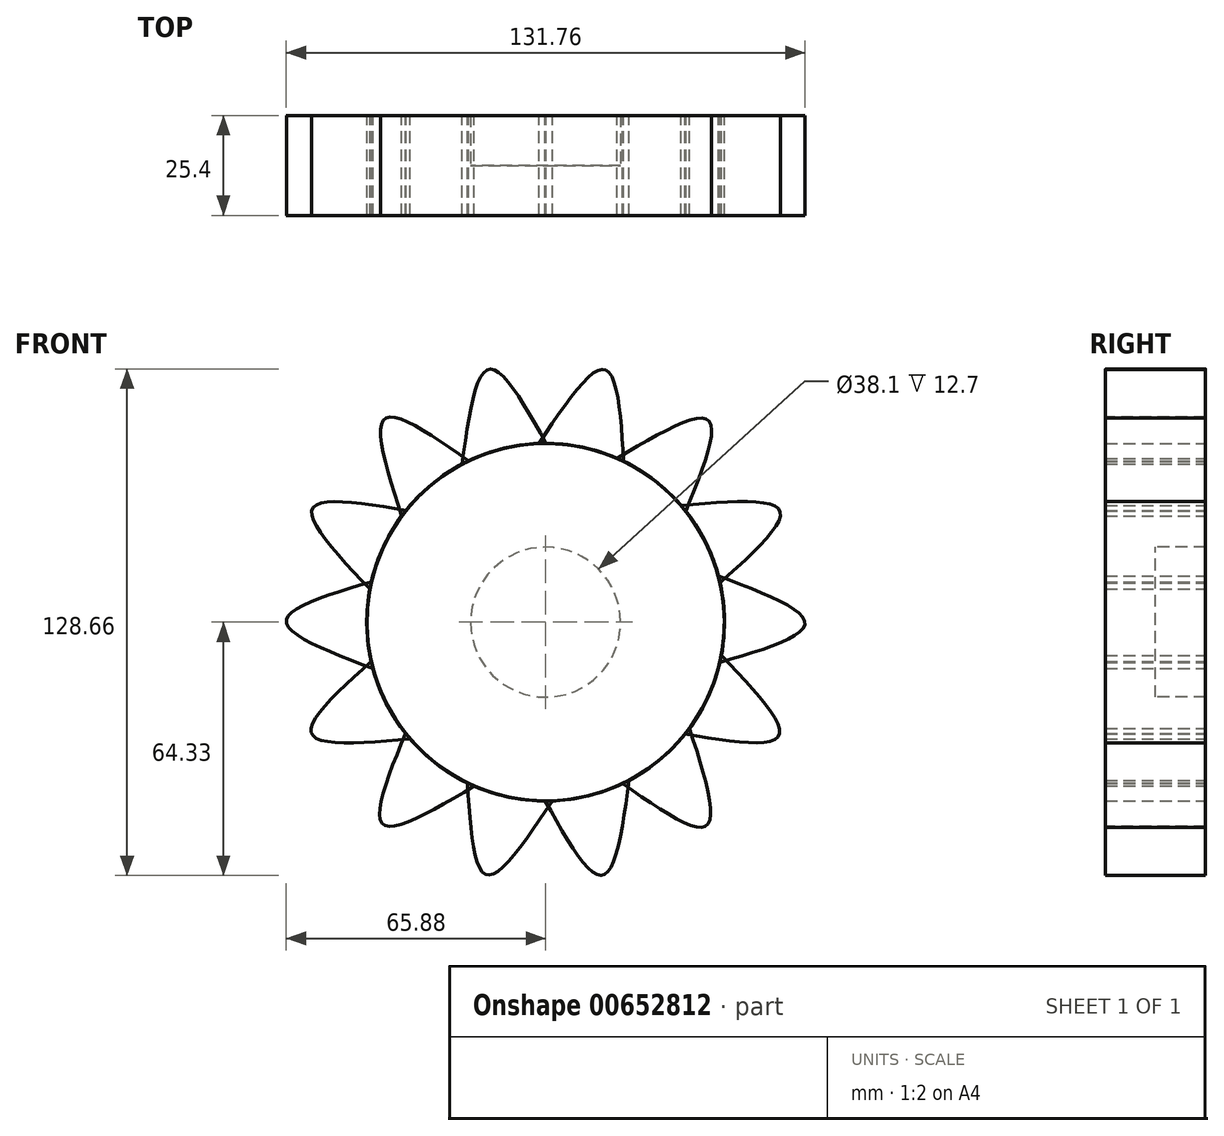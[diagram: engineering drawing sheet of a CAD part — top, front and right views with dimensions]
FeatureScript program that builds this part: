
annotation { "Feature Type Name" : "Feature", "Feature Type Description" : "" }
export const myFeature = defineFeature(function(context is Context, id is Id, definition is map)
    precondition{}
    {
        {
            var Q0;
            Q0=qCreatedBy(makeId("Front.planeOp"),FACE);
            var sketch = newSketch(context, id + "F0", { "sketchPlane" : qUnion([Q0])});
            skCircle(sketch, "E0", {"center": v(0, 0) * mm, "radius": 45.43 * mm});
            skFitSpline(sketch, "E1", {"points": [v(-36.56, 26.96) * mm, v(-40.82, 51.7) * mm, v(-19.6, 40.98) * mm], "startDerivative": vector(-21.52, 66.77) * mm, "endDerivative": vector(55.77, -39.2) * mm});
            skSolve(sketch);
        }
        {
            var Q0;
            Q0=qSketchRegion(id+"F0",true);
            extrude(context, id + "F1", {"entities" : qUnion([Q0]), "endBound" : BoundingType.SYMMETRIC, "depth" : 25.4 * mm, "offsetDistance" : 25.4 * mm});
        }
        {
            var Q0;
            Q0=makeQuery(id+"F1.opExtrude","SWEPT_BODY",BODY,{"disambiguationData":[OSD([sQuery(id+"F0.wireOp",EDGE,"E0"),sQuery(id+"F0.wireOp",EDGE,"E1")])]});
            var Q1;
            Q1=makeQuery(id+"F1.opExtrude","CAP_EDGE",EDGE,{"disambiguationData":[OSD([sQuery(id+"F0.wireOp",EDGE,"E0")])],"isStart":false});
            circularPattern(context, id + "F2", {"entities" : qUnion([Q0]), "axis" : qUnion([Q1]), "angle" : 360 * degree, "instanceCount" : 14, "equalSpace" : true});
        }
        {
            var Q0;
            Q0=qCreatedBy(makeId("Front.planeOp"),FACE);
            var sketch = newSketch(context, id + "F3", { "sketchPlane" : qUnion([Q0])});
            skCircle(sketch, "E2", {"center": v(0, 0) * mm, "radius": 25.92 * mm});
            skSolve(sketch);
        }
        {
            var Q0;
            Q0=sQuery(id+"F3.wireOp",VERTEX,"E2.center");
            var Q1;
            Q1=makeQuery(id+"F2.opPattern","COPY",BODY,{"derivedFrom":makeQuery(id+"F1.opExtrude","SWEPT_BODY",BODY,{"disambiguationData":[OSD([sQuery(id+"F0.wireOp",EDGE,"E0"),sQuery(id+"F0.wireOp",EDGE,"E1")])]}),"instanceName":"10"});
            hole(context, id + "F4", {"style" : HoleStyle.SIMPLE, "endStyle" : HoleEndStyle.THROUGH, "holeDiameter" : 38.1 * mm, "majorDiameter" : 6.35 * mm, "isTappedThrough" : true, "tappedDepth" : 12.7 * mm, "tapClearance" : 3, "locations" : qUnion([Q0]), "scope" : qUnion([Q1])});
        }
    });
